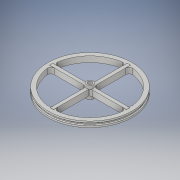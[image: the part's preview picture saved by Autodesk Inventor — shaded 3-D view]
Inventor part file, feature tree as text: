
AUTODESK INVENTOR PART (.ipt)
format: ipt  version: 2018 (Build 220112000, 112)  size: 231,936 bytes
history: native  units: in
note: dims shown in document units (in); Inventor stores cm internally (conversion verified against a paired STEP export)
features: sketch x10, extrude x9, fillet x5
ambient origin geometry x8: Origin, YZ Plane, XZ Plane, XY Plane, X Axis, Y Axis, Z Axis, Center Point
bodies: Solid1 (feature_tree)
feature tree (24):
  extrude  "Extrusion1"  Depth=0.0938in TaperAngle=0.0deg
  sketch  "Sketch2"  dims[d3=3.188in d4=0.0625in d5=0.0in]
  sketch  "Sketch3"  dims[d6=3.188in d7=0.0625in d8=0.0in d9=0.03in]
  extrude  "Extrusion2"  Depth=0.0625in TaperAngle=0.0deg
  extrude  "Extrusion3"  Depth=0.0625in TaperAngle=0.0deg
  fillet  "Fillet1"  Radius=0.03in
  extrude  "Extrusion4"  Depth=0.25in TaperAngle=0.0deg
  extrude  "Extrusion5"  Depth=0.225in TaperAngle=0.0deg
  extrude  "Extrusion6"  Depth=0.225in TaperAngle=0.0deg
  fillet  "Fillet2"  Radius=0.125in
  fillet  "Fillet3"  Radius=0.125in
  fillet  "Fillet4"  Radius=0.125in
  extrude  "Extrusion7"  Depth=0.225in TaperAngle=0.0deg
  extrude  "Extrusion8"  Depth=0.225in TaperAngle=0.0deg
  extrude  "Extrusion9"  Depth=0.125in
  fillet  "Fillet5"  [1 undecoded]
  sketch  "Sketch1"  dims[d0=3.125in d1=0.0938in d2=0.0in]
  sketch  "Sketch4"  dims[d10=2.875in d11=0.25in d12=0.0in]
  sketch  "Sketch5"  dims[d13=0.125in d14=0.225in d15=0.0in]
  sketch  "Sketch6"  dims[d16=0.125in d17=0.225in d18=0.0in d19=0.125in d20=0.125in d21=0.125in]
  sketch  "Sketch7"  dims[d22=0.25in d23=0.225in d24=0.0in]
  sketch  "Sketch8"  dims[d25=0.157in d26=0.225in d27=0.0in]
  sketch  "Sketch9"  dims[d28=0.125in d29=0.35in d30=0.0in d31=0.0in d32=0.125in]
  sketch  "Sketch10"
note: 1 required parameter value undecoded (feature->parameter linkage not recoverable at this tier; creation-order binding heuristic only, values carry confidence <= 0.55)
